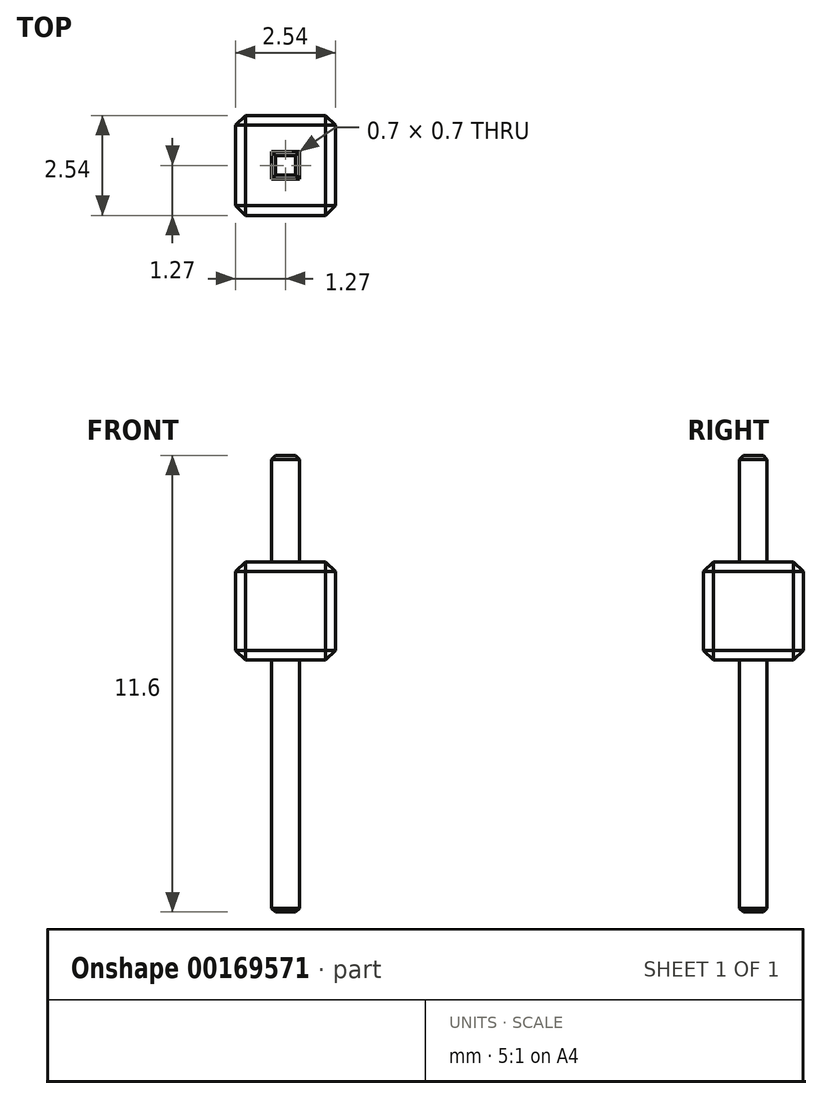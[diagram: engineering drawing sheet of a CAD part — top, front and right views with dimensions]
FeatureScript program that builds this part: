
annotation { "Feature Type Name" : "Feature", "Feature Type Description" : "" }
export const myFeature = defineFeature(function(context is Context, id is Id, definition is map)
    precondition{}
    {
        {
            var Q0;
            Q0=qCreatedBy(makeId("Top.planeOp"),FACE);
            var sketch = newSketch(context, id + "F0", { "sketchPlane" : qUnion([Q0])});
            skLineSegment(sketch, "E0.bottom", {"start": v(1.27, 1.27) * mm, "end": v(-1.27, 1.27) * mm});
            skLineSegment(sketch, "E0.top", {"start": v(1.27, -1.27) * mm, "end": v(-1.27, -1.27) * mm});
            skLineSegment(sketch, "E0.left", {"start": v(1.27, 1.27) * mm, "end": v(1.27, -1.27) * mm});
            skLineSegment(sketch, "E0.right", {"start": v(-1.27, 1.27) * mm, "end": v(-1.27, -1.27) * mm});
            skPoint(sketch, "E0.middle", {"position": v(0, 0) * mm});
            skSolve(sketch);
        }
        {
            var Q0;
            Q0=makeQuery(id+"F0.imprint","IMPRINT",FACE,{"disambiguationData":[TD([[makeQuery(id+"F0.imprint","IMPRINT",EDGE,{"derivedFrom":sQuery(id+"F0.wireOp",EDGE,"E0.bottom")}),1.0]])]});
            extrude(context, id + "F1", {"entities" : qUnion([Q0]), "depth" : 2.5 * mm, "offsetDistance" : 25 * mm});
        }
        {
            var Q0;
            Q0=makeQuery(id+"F1.opExtrude","SWEPT_EDGE",EDGE,{"disambiguationData":[OSD([sQuery(id+"F0.wireOp",EDGE,"E0.top"),sQuery(id+"F0.wireOp",EDGE,"E0.right")])]});
            var Q1;
            Q1=makeQuery(id+"F1.opExtrude","SWEPT_EDGE",EDGE,{"disambiguationData":[OSD([sQuery(id+"F0.wireOp",EDGE,"E0.top"),sQuery(id+"F0.wireOp",EDGE,"E0.left")])]});
            var Q2;
            Q2=makeQuery(id+"F1.opExtrude","SWEPT_EDGE",EDGE,{"disambiguationData":[OSD([sQuery(id+"F0.wireOp",EDGE,"E0.bottom"),sQuery(id+"F0.wireOp",EDGE,"E0.left")])]});
            var Q3;
            Q3=makeQuery(id+"F1.opExtrude","SWEPT_EDGE",EDGE,{"disambiguationData":[OSD([sQuery(id+"F0.wireOp",EDGE,"E0.bottom"),sQuery(id+"F0.wireOp",EDGE,"E0.right")])]});
            var Q4;
            Q4=makeQuery(id+"F1.opExtrude","CAP_EDGE",EDGE,{"disambiguationData":[OSD([sQuery(id+"F0.wireOp",EDGE,"E0.bottom")])],"isStart":false});
            var Q5;
            Q5=makeQuery(id+"F1.opExtrude","CAP_EDGE",EDGE,{"disambiguationData":[OSD([sQuery(id+"F0.wireOp",EDGE,"E0.left")])],"isStart":false});
            var Q6;
            Q6=makeQuery(id+"F1.opExtrude","CAP_EDGE",EDGE,{"disambiguationData":[OSD([sQuery(id+"F0.wireOp",EDGE,"E0.top")])],"isStart":false});
            var Q7;
            Q7=makeQuery(id+"F1.opExtrude","CAP_EDGE",EDGE,{"disambiguationData":[OSD([sQuery(id+"F0.wireOp",EDGE,"E0.right")])],"isStart":false});
            var Q8;
            Q8=makeQuery(id+"F1.opExtrude","CAP_EDGE",EDGE,{"disambiguationData":[OSD([sQuery(id+"F0.wireOp",EDGE,"E0.left")])],"isStart":true});
            var Q9;
            Q9=makeQuery(id+"F1.opExtrude","CAP_EDGE",EDGE,{"disambiguationData":[OSD([sQuery(id+"F0.wireOp",EDGE,"E0.top")])],"isStart":true});
            var Q10;
            Q10=makeQuery(id+"F1.opExtrude","CAP_EDGE",EDGE,{"disambiguationData":[OSD([sQuery(id+"F0.wireOp",EDGE,"E0.right")])],"isStart":true});
            var Q11;
            Q11=makeQuery(id+"F1.opExtrude","CAP_EDGE",EDGE,{"disambiguationData":[OSD([sQuery(id+"F0.wireOp",EDGE,"E0.bottom")])],"isStart":true});
            chamfer(context, id + "F2", {"entities" : qUnion([Q0, Q1, Q2, Q3, Q4, Q5, Q6, Q7, Q8, Q9, Q10, Q11]), "width" : 0.25 * mm, "tangentPropagation" : true});
        }
        {
            var Q0;
            Q0=makeQuery(id+"F1.opExtrude","CAP_FACE",FACE,{"disambiguationData":[OSD([sQuery(id+"F0.wireOp",EDGE,"E0.bottom"),sQuery(id+"F0.wireOp",EDGE,"E0.top"),sQuery(id+"F0.wireOp",EDGE,"E0.left"),sQuery(id+"F0.wireOp",EDGE,"E0.right")])],"isStart":false});
            var sketch = newSketch(context, id + "F3", { "sketchPlane" : qUnion([Q0])});
            skLineSegment(sketch, "E1", {"start": v(-1.02, 1.02) * mm, "end": v(1.02, -1.02) * mm, "construction": true});
            skLineSegment(sketch, "E2", {"start": v(1.02, 1.02) * mm, "end": v(-1.02, -1.02) * mm, "construction": true});
            skLineSegment(sketch, "E3.bottom", {"start": v(-0.35, 0.35) * mm, "end": v(0.35, 0.35) * mm});
            skLineSegment(sketch, "E3.top", {"start": v(-0.35, -0.35) * mm, "end": v(0.35, -0.35) * mm});
            skLineSegment(sketch, "E3.left", {"start": v(-0.35, 0.35) * mm, "end": v(-0.35, -0.35) * mm});
            skLineSegment(sketch, "E3.right", {"start": v(0.35, 0.35) * mm, "end": v(0.35, -0.35) * mm});
            skPoint(sketch, "E3.middle", {"position": v(0, 0) * mm});
            skSolve(sketch);
        }
        {
            var Q0;
            Q0 = qSketchRegion(id + "F3", true);
            var Q1;
            Q1 = qConstructionFilter(qBodyType(qCreatedBy(id + "F3" ,EDGE), BodyType.WIRE), ConstructionObject.NO);
            extrude(context, id + "F4", {"entities" : qUnion([Q0]), "operationType" : NewBodyOperationType.ADD, "surfaceEntities" : qUnion([Q1]), "depth" : 2.7 * mm, "offsetDistance" : 25 * mm, "hasSecondDirection" : true, "secondDirectionOppositeDirection" : true, "secondDirectionDepth" : 8.9 * mm});
        }
        {
            var Q0;
            Q0=makeQuery(id+"F4.opExtrude","CAP_EDGE",EDGE,{"disambiguationData":[OSD([sQuery(id+"F3.wireOp",EDGE,"E3.right")])],"isStart":false});
            var Q1;
            Q1=makeQuery(id+"F4.opExtrude","CAP_EDGE",EDGE,{"disambiguationData":[OSD([sQuery(id+"F3.wireOp",EDGE,"E3.bottom")])],"isStart":false});
            var Q2;
            Q2=makeQuery(id+"F4.opExtrude","CAP_EDGE",EDGE,{"disambiguationData":[OSD([sQuery(id+"F3.wireOp",EDGE,"E3.left")])],"isStart":false});
            var Q3;
            Q3=makeQuery(id+"F4.opExtrude","CAP_EDGE",EDGE,{"disambiguationData":[OSD([sQuery(id+"F3.wireOp",EDGE,"E3.top")])],"isStart":false});
            var Q4;
            Q4=makeQuery(id+"F4.opExtrude","CAP_EDGE",EDGE,{"disambiguationData":[OSD([sQuery(id+"F3.wireOp",EDGE,"E3.right")])],"isStart":true});
            var Q5;
            Q5=makeQuery(id+"F4.opExtrude","CAP_EDGE",EDGE,{"disambiguationData":[OSD([sQuery(id+"F3.wireOp",EDGE,"E3.top")])],"isStart":true});
            var Q6;
            Q6=makeQuery(id+"F4.opExtrude","CAP_EDGE",EDGE,{"disambiguationData":[OSD([sQuery(id+"F3.wireOp",EDGE,"E3.left")])],"isStart":true});
            var Q7;
            Q7=makeQuery(id+"F4.opExtrude","CAP_EDGE",EDGE,{"disambiguationData":[OSD([sQuery(id+"F3.wireOp",EDGE,"E3.bottom")])],"isStart":true});
            chamfer(context, id + "F5", {"entities" : qUnion([Q0, Q1, Q2, Q3, Q4, Q5, Q6, Q7]), "width" : 0.1 * mm, "tangentPropagation" : true});
        }
    });
